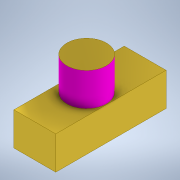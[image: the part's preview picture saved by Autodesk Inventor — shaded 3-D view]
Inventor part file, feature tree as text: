
AUTODESK INVENTOR PART (.ipt)
format: ipt  version: 2021 (Build 250183000, 183)  size: 102,912 bytes
history: native  units: mm
features: extrude x2, sketch x2
ambient origin geometry x8: Origin, YZ Plane, XZ Plane, XY Plane, X Axis, Y Axis, Z Axis, Center Point
bodies: Solid1 (feature_tree)
feature tree (4):
  extrude  "Extrusion1"  Depth=10.0mm TaperAngle=0.0deg
  extrude  "Extrusion2"  [1 undecoded]
  sketch  "Sketch1"  dims[d0=10.0mm d1=0.0mm d2=10.0mm d3=0.0mm]
  sketch  "Sketch2"
note: 1 required parameter value undecoded (feature->parameter linkage not recoverable at this tier; creation-order binding heuristic only, values carry confidence <= 0.55)
